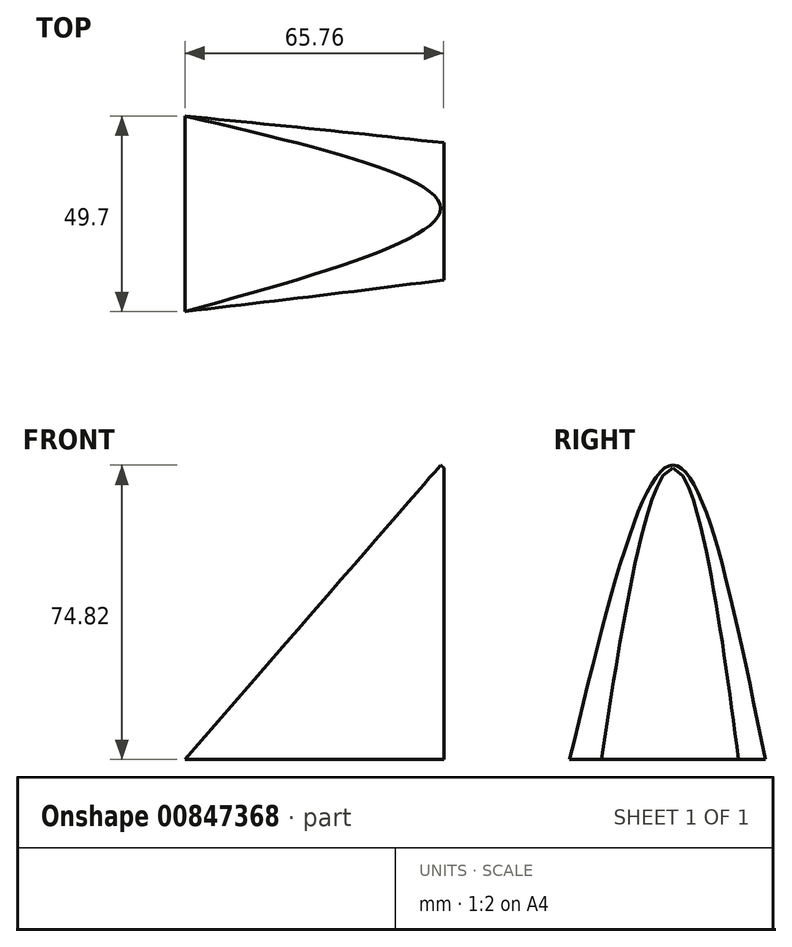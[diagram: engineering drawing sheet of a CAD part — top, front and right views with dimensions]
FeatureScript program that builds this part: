
annotation { "Feature Type Name" : "Feature", "Feature Type Description" : "" }
export const myFeature = defineFeature(function(context is Context, id is Id, definition is map)
    precondition{}
    {
        {
            var Q0;
            Q0=qCreatedBy(makeId("Front.planeOp"),FACE);
            var sketch = newSketch(context, id + "F0", { "sketchPlane" : qUnion([Q0])});
            skLineSegment(sketch, "E0", {"start": v(-2.49, -33.4) * mm, "end": v(-68.25, -33.4) * mm});
            skLineSegment(sketch, "E1", {"start": v(-2.49, -33.4) * mm, "end": v(-2.49, 42.35) * mm});
            skLineSegment(sketch, "E2", {"start": v(-2.49, 42.35) * mm, "end": v(-68.25, -33.4) * mm});
            skSolve(sketch);
        }
        {
            var Q0;
            Q0=qSketchRegion(id+"F0",true);
            extrude(context, id + "F1", {"entities" : qUnion([Q0]), "depth" : 76.2 * mm, "offsetDistance" : 25.4 * mm});
        }
        {
            var Q0;
            Q0=makeQuery(id+"F1.opExtrude","SWEPT_FACE",FACE,{"disambiguationData":[OSD([sQuery(id+"F0.wireOp",EDGE,"E2")])]});
            var sketch = newSketch(context, id + "F2", { "sketchPlane" : qUnion([Q0])});
            skLineSegment(sketch, "E3", {"start": v(38.1, -69.96) * mm, "end": v(38.1, 29.12) * mm});
            skLineSegment(sketch, "E4", {"start": v(14.68, -69.96) * mm, "end": v(64.38, -69.96) * mm});
            skFitSpline(sketch, "E5", {"points": [v(64.38, -69.96) * mm, v(38.1, 29.12) * mm, v(14.68, -69.96) * mm], "startDerivative": vector(-53.86, 297.09) * mm, "endDerivative": vector(-45.54, -297.42) * mm});
            skSolve(sketch);
        }
        {
            var Q0;
            {var subQ0=sQuery(id+"F0.wireOp",EDGE,"E2");var subQ1=makeQuery(id+"F1.opExtrude","CAP_EDGE",EDGE,{"disambiguationData":[OSD([subQ0])],"isStart":true});Q0=makeQuery(id+"F2.imprint","IMPRINT",FACE,{"disambiguationData":[TD([[makeQuery(id+"F2.imprint","IMPRINT",EDGE,{"derivedFrom":subQ1}),1.0]])]});}
            extrude(context, id + "F3", {"entities" : qUnion([Q0]), "operationType" : NewBodyOperationType.REMOVE, "endBound" : BoundingType.THROUGH_ALL, "oppositeDirection" : true, "depth" : 71.37 * mm, "offsetDistance" : 25.4 * mm});
        }
    });
